# Revit family: IS_LDV_E2634_BIM_GB
name_source: partatom
category: Plumbing Fixtures
units: mm (PartAtom-declared; Revit-internal decimal feet)

## family parameters
Cut with Voids When Loaded = No
Host = Face
Maintain Annotation Orientation = No
OmniClass Number = 23.45.05.21.11.11
OmniClass Title = Water Operated Water Closets
Part Type = Normal
Room Calculation Point = No
Round Connector Dimension = Use Diameter
Shared = Yes

## types (2) — shared parameters
Accessories = https://www.idealstandard.co.uk
AreaUnits = millimeters
Assembly Code = C1030200
AssetType = Fixed
BIMObjectName = IS_LDV_WCPan_E2634
BREEAMApproved = No
Brand = Ideal Standard
ConnectionType = Plumbing
Default Elevation = 400 mm  [stored 1.31234 ft]
DurationUnit = year
ECA = No
EPD = https://www.idealstandard.co.uk
ExpectedLife = 30
Help = https://www.idealstandard.co.uk
IfcExportAs = IfcSanitaryTerminalType
IfcExportType = TOILETPAN
InstallationInstructions = https://www.idealstandard.co.uk
LinearUnits = millimeters
MAT = Ceramic_White_01
Manufacturer = Ideal Standard
ManufacturerURL = https://www.idealstandard.co.uk
NBSDescription = WC pans
NBSReference = Pr_40_20_93_94
Name = WCPan_LDV_E2634_IdealStandard
NettWeight = 26,5
NominalDepth = 541 mm
NominalHeight = 339 mm
NominalLength = 541 mm
NominalWidth = 360 mm
PanColor = White
PanMaterial = Vitreous china
PanMounting = BackToWall
ProductInformation = https://www.idealstandard.co.uk
Shape = Sculptured
Size = 360 x 541 x339 mm
Space = Internal
ToiletPanType = WashDown
ToiletType = Other
URL = https://www.idealstandard.co.uk
Uniclass2015Code = Pr_40_20_93_94
Uniclass2015Description = WC pans
Uniclass2015Title = WC pans
Uniclass2015Version = Products v1.33
Version = 1
VolumeUnits = Litres
WRAS = No
WarrantyDescription = Manufacturers Warranty
WarrantyDurationParts = 99
WarrantyDurationUnit = year
WarrantyGuarantorParts = Ideal Standard
WaterEfficientProduct = No
zero-valued in all types: CWFU, Cost, HWFU, SpilloverLevel, WFU

## per-type parameters (varying)
| type | BarCode | Description | Features | Finish | Model | ModelNumber | ModelReference |
| E263401 - LDV WHG BOWL HF AB WHITE BXD | 5017830562443 | La Dolce Vita® wallhung bowl, Aquablade, hidden fixation, incl. Easyfix+ WW966066, white | La Dolce Vita® wallhung bowl, Aquablade, hidden fixation, incl. Easyfix+ WW966066, white, carton box, EU pallet | white | E263401 | E263401 | La Dolce Vita® wallhung bowl, Aquablade, hidden fixation, incl. Easyfix+ WW966066, white |
| E2634MA - LDV WHG BWL HF AB WHT IP BXD | 5017830563860 | La Dolce Vita® wallhung bowl, Aquablade, hidden fixation,incl. Easyfix+ WW966066, white Ideal Plus | La Dolce Vita® wallhung bowl, Aquablade, hidden fixation,incl. Easyfix+ WW966066, white Ideal Plus, carton box, EU pallet | white Ideal Plus | E2634MA | E2634MA | La Dolce Vita® wallhung bowl, Aquablade, hidden fixation,incl. Easyfix+ WW966066, white Ideal Plus |

note: [stored X ft] marks values corroborated as IEEE doubles in the binary element streams (Revit-internal decimal feet)

## geometry (parser evidence)
native form markers: Sweep x3
no freeform markers — native parametric forms only
